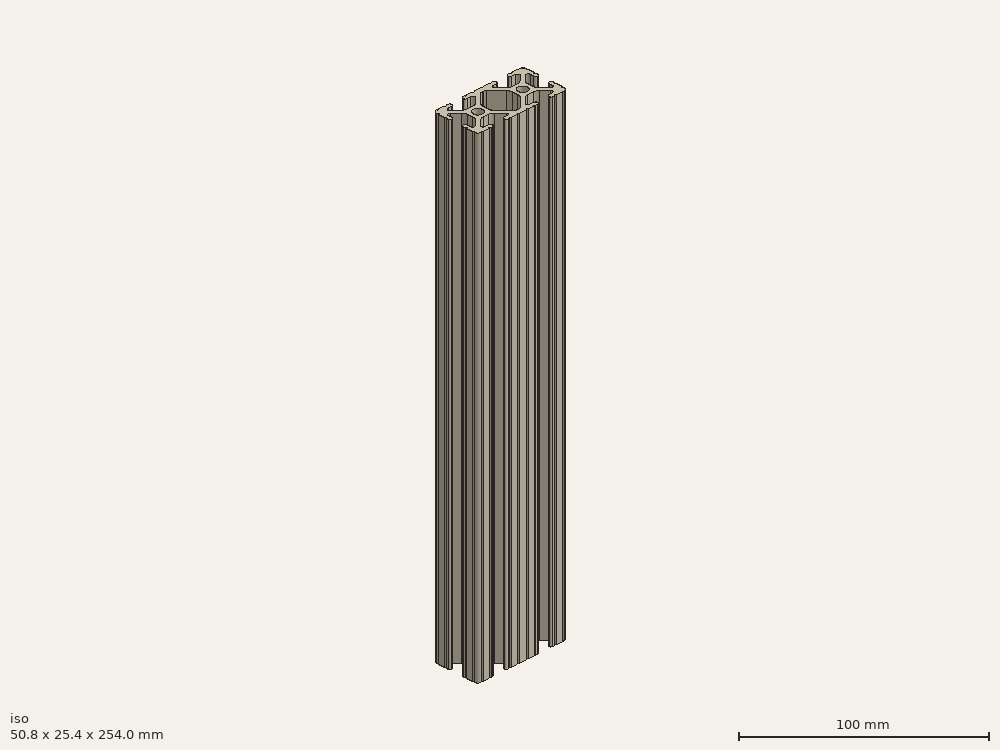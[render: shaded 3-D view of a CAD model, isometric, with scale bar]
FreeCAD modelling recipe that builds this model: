
FCSTD DOCUMENT  (FreeCAD 0.19R23756 (Git))
Label: 1020-10
License: All rights reserved
LicenseURL: http://en.wikipedia.org/wiki/All_rights_reserved
objects: Sketcher::SketchObject×1, Part::Extrusion×1
note: 2 computed .brp shape members not serialized (recipe doc carries the construction recipe); baked Part::Feature solids carry a one-line shape summary decoded from their .brp

FEATURE [Sketcher::SketchObject] Sketch162
  FullyConstrained = false
  sketch-geometry (162):
    g0: LineSegment StartX=7.25951 StartY=3.86941 StartZ=0 EndX=1.54575 EndY=9.57277 EndZ=0
    g1: LineSegment StartX=8.41248 StartY=-10.4902 StartZ=0 EndX=6.28364 EndY=-10.4902 EndZ=0
    g2: ArcOfCircle CenterX=8.41255 CenterY=-11.651 CenterZ=0 NormalX=0 NormalY=0 NormalZ=1 AngleXU=0 Radius=1.04895 StartAngle=4.71239 EndAngle=6.28319
    g3: LineSegment StartX=5.53258 StartY=-8.66607 StartZ=0 EndX=8.80999 EndY=-5.41626 EndZ=0
    g4: LineSegment StartX=9.4615 StartY=-11.651 StartZ=0 EndX=9.4615 EndY=-11.5392 EndZ=0
    g5: ArcOfCircle CenterX=8.41248 CenterY=-11.5392 CenterZ=0 NormalX=0 NormalY=0 NormalZ=1 AngleXU=0 Radius=1.04902 StartAngle=1.15714e-07 EndAngle=1.5708
    g6: ArcOfCircle CenterX=6.28364 CenterY=-9.42351 CenterZ=0 NormalX=0 NormalY=0 NormalZ=1 AngleXU=0 Radius=1.06669 StartAngle=2.35197 EndAngle=4.71239
    g7: LineSegment StartX=-7.28286 StartY=-3.84586 StartZ=0 EndX=-1.67557 EndY=-9.56109 EndZ=0
    g8: LineSegment StartX=1.50403 StartY=-9.57645 StartZ=0 EndX=7.25205 EndY=-3.87684 EndZ=0
    g9: LineSegment StartX=-0.551457 StartY=-10.033 StartZ=0 EndX=0.3952 EndY=-10.033 EndZ=0
    g10: LineSegment StartX=-1.54575 StartY=9.57277 StartZ=0 EndX=-7.25951 EndY=3.86941 EndZ=0
    g11: ArcOfCircle CenterX=0.3952 CenterY=-8.4582 CenterZ=0 NormalX=0 NormalY=0 NormalZ=1 AngleXU=0 Radius=1.5748 StartAngle=4.71239 EndAngle=5.49356
    g12: ArcOfCircle CenterX=5.0165 CenterY=-1.6223 CenterZ=0 NormalX=0 NormalY=0 NormalZ=1 AngleXU=0 Radius=3.175 StartAngle=5.49356 EndAngle=6.28319
    g13: LineSegment StartX=8.1915 StartY=-1.6223 StartZ=0 EndX=8.1915 EndY=1.6223 EndZ=0
    g14: LineSegment StartX=0.433213 StartY=10.033 StartZ=0 EndX=-0.433213 EndY=10.033 EndZ=0
    g15: ArcOfCircle CenterX=-0.551456 CenterY=-8.4582 CenterZ=0 NormalX=0 NormalY=0 NormalZ=1 AngleXU=0 Radius=1.5748 StartAngle=3.91746 EndAngle=4.71239
    g16: ArcOfCircle CenterX=-5.0165 CenterY=1.6223 CenterZ=0 NormalX=0 NormalY=0 NormalZ=1 AngleXU=0 Radius=3.175 StartAngle=2.35528 EndAngle=3.14159
    g17: ArcOfCircle CenterX=-0.433213 CenterY=8.4582 CenterZ=0 NormalX=0 NormalY=0 NormalZ=1 AngleXU=0 Radius=1.5748 StartAngle=1.5708 EndAngle=2.35528
    g18: ArcOfCircle CenterX=5.0165 CenterY=1.6223 CenterZ=0 NormalX=0 NormalY=0 NormalZ=1 AngleXU=0 Radius=3.175 StartAngle=2.15656e-07 EndAngle=0.78631
    g19: Circle CenterX=12.7 CenterY=-2.5e-15 CenterZ=0 NormalX=0 NormalY=0 NormalZ=-1 AngleXU=0 Radius=2.6035
    g20: Circle CenterX=-12.7 CenterY=2.5e-15 CenterZ=0 NormalX=0 NormalY=0 NormalZ=-1 AngleXU=0 Radius=2.6035
    g21: LineSegment StartX=-8.1915 StartY=1.6223 StartZ=0 EndX=-8.1915 EndY=-1.6223 EndZ=0
    g22: LineSegment StartX=-2.13358 StartY=-12.7 StartZ=0 EndX=2.13358 EndY=-12.7 EndZ=0
    g23: ArcOfCircle CenterX=-5.0165 CenterY=-1.6223 CenterZ=0 NormalX=0 NormalY=0 NormalZ=1 AngleXU=0 Radius=3.175 StartAngle=3.14159 EndAngle=3.91746
    g24: LineSegment StartX=3.14958 StartY=-12.7 StartZ=0 EndX=6.3669 EndY=-12.7 EndZ=0
    g25: ArcOfCircle CenterX=6.8749 CenterY=-12.7 CenterZ=0 NormalX=0 NormalY=0 NormalZ=1 AngleXU=0 Radius=0.508 StartAngle=0 EndAngle=3.14159
    g26: LineSegment StartX=-6.28939 StartY=-10.4902 StartZ=0 EndX=-8.41248 EndY=-10.4902 EndZ=0
    g27: LineSegment StartX=-8.41255 StartY=-12.7 StartZ=0 EndX=-7.38288 EndY=-12.7 EndZ=0
    g28: ArcOfCircle CenterX=0.433213 CenterY=8.4582 CenterZ=0 NormalX=0 NormalY=0 NormalZ=1 AngleXU=0 Radius=1.5748 StartAngle=0.78631 EndAngle=1.5708
    g29: ArcOfCircle CenterX=2.64158 CenterY=-12.7 CenterZ=0 NormalX=0 NormalY=0 NormalZ=1 AngleXU=0 Radius=0.508 StartAngle=0 EndAngle=3.14159
    g30: ArcOfCircle CenterX=-16.9875 CenterY=-11.5392 CenterZ=0 NormalX=0 NormalY=0 NormalZ=1 AngleXU=0 Radius=1.04902 StartAngle=1.16223e-07 EndAngle=1.5708
    g31: LineSegment StartX=-8.81696 StartY=-5.44724 StartZ=0 EndX=-5.56415 EndY=-8.76265 EndZ=0
    g32: LineSegment StartX=-16.9875 StartY=-10.4902 StartZ=0 EndX=-19.1164 EndY=-10.4902 EndZ=0
    g33: ArcOfCircle CenterX=-11.0833 CenterY=-7.6708 CenterZ=0 NormalX=0 NormalY=0 NormalZ=1 AngleXU=0 Radius=3.175 StartAngle=0.775866 EndAngle=1.5708
    g34: ArcOfCircle CenterX=-14.3449 CenterY=-7.6708 CenterZ=0 NormalX=0 NormalY=0 NormalZ=1 AngleXU=0 Radius=3.175 StartAngle=1.5708 EndAngle=2.3692
    g35: ArcOfCircle CenterX=-19.1164 CenterY=-9.4742 CenterZ=0 NormalX=0 NormalY=0 NormalZ=1 AngleXU=0 Radius=1.016 StartAngle=2.3692 EndAngle=4.71239
    g36: ArcOfCircle CenterX=-8.41248 CenterY=-11.5392 CenterZ=0 NormalX=0 NormalY=0 NormalZ=1 AngleXU=0 Radius=1.04902 StartAngle=1.5708 EndAngle=3.14159
    g37: LineSegment StartX=7.3829 StartY=-12.7 StartZ=0 EndX=8.41255 EndY=-12.7 EndZ=0
    g38: ArcOfCircle CenterX=-8.41255 CenterY=-11.651 CenterZ=0 NormalX=0 NormalY=0 NormalZ=1 AngleXU=0 Radius=1.04895 StartAngle=3.14159 EndAngle=4.71239
    g39: ArcOfCircle CenterX=14.3545 CenterY=-7.6708 CenterZ=0 NormalX=0 NormalY=0 NormalZ=1 AngleXU=0 Radius=3.175 StartAngle=0.789627 EndAngle=1.5708
    g40: ArcOfCircle CenterX=20.3835 CenterY=-1.55362 CenterZ=0 NormalX=0 NormalY=0 NormalZ=1 AngleXU=0 Radius=3.175 StartAngle=3.14159 EndAngle=3.93122
    g41: LineSegment StartX=23.1902 StartY=6.498 StartZ=0 EndX=23.1902 EndY=4.28752 EndZ=0
    g42: LineSegment StartX=-14.3449 StartY=-4.4958 StartZ=0 EndX=-11.0833 EndY=-4.4958 EndZ=0
    g43: LineSegment StartX=-19.8441 StartY=-8.76517 StartZ=0 EndX=-16.619 EndY=-5.45511 EndZ=0
    g44: LineSegment StartX=-6.36688 StartY=-12.7 StartZ=0 EndX=-3.14958 EndY=-12.7 EndZ=0
    g45: ArcOfCircle CenterX=-6.28939 CenterY=-9.4742 CenterZ=0 NormalX=0 NormalY=0 NormalZ=1 AngleXU=0 Radius=1.016 StartAngle=4.71239 EndAngle=7.05905
    g46: LineSegment StartX=-9.4615 StartY=-11.5392 StartZ=0 EndX=-9.4615 EndY=-11.6511 EndZ=0
    g47: ArcOfCircle CenterX=-6.87488 CenterY=-12.7 CenterZ=0 NormalX=0 NormalY=0 NormalZ=1 AngleXU=0 Radius=0.508 StartAngle=0 EndAngle=3.14159
    g48: LineSegment StartX=-15.9385 StartY=-11.651 StartZ=0 EndX=-15.9385 EndY=-11.5392 EndZ=0
    g49: ArcOfCircle CenterX=-2.64158 CenterY=-12.7 CenterZ=0 NormalX=0 NormalY=0 NormalZ=1 AngleXU=0 Radius=0.508 StartAngle=0 EndAngle=3.14159
    g50: ArcOfCircle CenterX=22.1596 CenterY=-6.33474 CenterZ=0 NormalX=0 NormalY=0 NormalZ=1 AngleXU=0 Radius=1.03057 StartAngle=3.93122 EndAngle=6.28319
    g51: ArcOfCircle CenterX=25.4 CenterY=5.82513 CenterZ=0 NormalX=0 NormalY=0 NormalZ=1 AngleXU=0 Radius=0.508 StartAngle=1.5708 EndAngle=4.71239
    g52: LineSegment StartX=25.4 StartY=6.33313 StartZ=0 EndX=25.4 EndY=9.5504 EndZ=0
    g53: LineSegment StartX=19.0331 StartY=-12.7 StartZ=0 EndX=22.2504 EndY=-12.7 EndZ=0
    g54: ArcOfCircle CenterX=20.3835 CenterY=1.69518 CenterZ=0 NormalX=0 NormalY=0 NormalZ=1 AngleXU=0 Radius=3.175 StartAngle=2.35528 EndAngle=3.14159
    g55: LineSegment StartX=16.9875 StartY=-12.7 StartZ=0 EndX=18.0171 EndY=-12.7 EndZ=0
    g56: ArcOfCircle CenterX=23.2918 CenterY=10.5918 CenterZ=0 NormalX=0 NormalY=0 NormalZ=1 AngleXU=0 Radius=2.1082 StartAngle=6.27114 EndAngle=7.86603
    g57: ArcOfCircle CenterX=24.2392 CenterY=-4.28752 CenterZ=0 NormalX=0 NormalY=0 NormalZ=1 AngleXU=0 Radius=1.04902 StartAngle=1.5708 EndAngle=3.14159
    g58: ArcOfCircle CenterX=24.401 CenterY=-4.23752 CenterZ=0 NormalX=0 NormalY=0 NormalZ=1 AngleXU=0 Radius=0.99902 StartAngle=1.41033e-07 EndAngle=1.5708
    g59: LineSegment StartX=16.59 StartY=-5.41626 StartZ=0 EndX=19.8674 EndY=-8.66607 EndZ=0
    g60: ArcOfCircle CenterX=16.9875 CenterY=-11.5392 CenterZ=0 NormalX=0 NormalY=0 NormalZ=1 AngleXU=0 Radius=1.04902 StartAngle=1.5708 EndAngle=3.14159
    g61: LineSegment StartX=22.2504 StartY=12.7 StartZ=0 EndX=19.0331 EndY=12.7 EndZ=0
    g62: ArcOfCircle CenterX=23.2918 CenterY=-10.5918 CenterZ=0 NormalX=0 NormalY=0 NormalZ=1 AngleXU=0 Radius=2.1082 StartAngle=4.70034 EndAngle=6.29523
    g63: ArcOfCircle CenterX=11.0455 CenterY=-7.6708 CenterZ=0 NormalX=0 NormalY=0 NormalZ=1 AngleXU=0 Radius=3.175 StartAngle=1.5708 EndAngle=2.35197
    g64: ArcOfCircle CenterX=22.7584 CenterY=12.7 CenterZ=0 NormalX=0 NormalY=0 NormalZ=1 AngleXU=0 Radius=0.508 StartAngle=3.14159 EndAngle=6.28288
    g65: LineSegment StartX=19.1164 StartY=-10.4902 StartZ=0 EndX=16.9875 EndY=-10.4902 EndZ=0
    g66: ArcOfCircle CenterX=22.7584 CenterY=-12.7 CenterZ=0 NormalX=0 NormalY=0 NormalZ=1 AngleXU=0 Radius=0.508 StartAngle=0.000301216 EndAngle=3.14159
    g67: ArcOfCircle CenterX=16.9875 CenterY=11.651 CenterZ=0 NormalX=0 NormalY=0 NormalZ=1 AngleXU=0 Radius=1.04902 StartAngle=1.5708 EndAngle=3.14159
    g68: ArcOfCircle CenterX=24.351 CenterY=4.28752 CenterZ=0 NormalX=0 NormalY=0 NormalZ=1 AngleXU=0 Radius=1.04902 StartAngle=4.71239 EndAngle=6.28319
    g69: ArcOfCircle CenterX=19.1164 CenterY=9.4742 CenterZ=0 NormalX=0 NormalY=0 NormalZ=1 AngleXU=0 Radius=1.016 StartAngle=5.49688 EndAngle=7.85398
    g70: LineSegment StartX=19.8341 StartY=8.75512 StartZ=0 EndX=16.4966 EndY=5.42369 EndZ=0
    g71: LineSegment StartX=18.0171 StartY=12.7 StartZ=0 EndX=16.9875 EndY=12.7 EndZ=0
    g72: ArcOfCircle CenterX=18.5251 CenterY=-12.7 CenterZ=0 NormalX=0 NormalY=0 NormalZ=1 AngleXU=0 Radius=0.508 StartAngle=0 EndAngle=3.14159
    g73: LineSegment StartX=15.9384 StartY=11.651 StartZ=0 EndX=15.9384 EndY=11.5392 EndZ=0
    g74: LineSegment StartX=16.9875 StartY=10.4902 StartZ=0 EndX=19.1164 EndY=10.4902 EndZ=0
    g75: LineSegment StartX=11.0455 StartY=-4.4958 StartZ=0 EndX=14.3545 EndY=-4.4958 EndZ=0
    g76: ArcOfCircle CenterX=14.2536 CenterY=7.6708 CenterZ=0 NormalX=0 NormalY=0 NormalZ=1 AngleXU=0 Radius=3.175 StartAngle=4.71239 EndAngle=5.49688
    g77: ArcOfCircle CenterX=25.4 CenterY=-5.82508 CenterZ=0 NormalX=0 NormalY=0 NormalZ=1 AngleXU=0 Radius=0.508 StartAngle=1.5708 EndAngle=4.71239
    g78: LineSegment StartX=18.1405 StartY=3.94229 StartZ=0 EndX=21.4316 EndY=7.22739 EndZ=0
    g79: LineSegment StartX=25.4 StartY=-5.31708 StartZ=0 EndX=25.4 EndY=-4.23752 EndZ=0
    g80: LineSegment StartX=14.2536 StartY=4.4958 StartZ=0 EndX=11.1464 EndY=4.4958 EndZ=0
    g81: ArcOfCircle CenterX=18.5251 CenterY=12.7 CenterZ=0 NormalX=0 NormalY=0 NormalZ=1 AngleXU=0 Radius=0.508 StartAngle=3.14159 EndAngle=6.28319
    g82: LineSegment StartX=23.1902 StartY=-4.28752 StartZ=0 EndX=23.1902 EndY=-6.33474 EndZ=0
    g83: LineSegment StartX=24.401 StartY=-3.2385 StartZ=0 EndX=24.2392 EndY=-3.2385 EndZ=0
    g84: ArcOfCircle CenterX=22.1596 CenterY=6.498 CenterZ=0 NormalX=0 NormalY=0 NormalZ=1 AngleXU=0 Radius=1.03057 StartAngle=0 EndAngle=2.35528
    g85: LineSegment StartX=15.9385 StartY=-11.5392 StartZ=0 EndX=15.9385 EndY=-11.6511 EndZ=0
    g86: LineSegment StartX=25.4 StartY=4.28752 StartZ=0 EndX=25.4 EndY=5.31713 EndZ=0
    g87: ArcOfCircle CenterX=11.1464 CenterY=7.6708 CenterZ=0 NormalX=0 NormalY=0 NormalZ=1 AngleXU=0 Radius=3.175 StartAngle=3.9279 EndAngle=4.71239
    g88: LineSegment StartX=8.90339 StartY=5.42369 StartZ=0 EndX=5.56588 EndY=8.75512 EndZ=0
    g89: LineSegment StartX=21.434 StartY=-7.06654 StartZ=0 EndX=18.148 EndY=-3.80816 EndZ=0
    g90: ArcOfCircle CenterX=25.4 CenterY=10.0584 CenterZ=0 NormalX=0 NormalY=0 NormalZ=1 AngleXU=0 Radius=0.508 StartAngle=1.5711 EndAngle=4.71239
    g91: ArcOfCircle CenterX=16.9875 CenterY=-11.651 CenterZ=0 NormalX=0 NormalY=0 NormalZ=1 AngleXU=0 Radius=1.04895 StartAngle=3.14159 EndAngle=4.71239
    g92: ArcOfCircle CenterX=19.1164 CenterY=-9.42352 CenterZ=0 NormalX=0 NormalY=0 NormalZ=1 AngleXU=0 Radius=1.06668 StartAngle=4.71239 EndAngle=7.07281
    g93: ArcOfCircle CenterX=24.2392 CenterY=4.28752 CenterZ=0 NormalX=0 NormalY=0 NormalZ=1 AngleXU=0 Radius=1.04902 StartAngle=3.14159 EndAngle=4.71239
    g94: ArcOfCircle CenterX=16.9875 CenterY=11.5392 CenterZ=0 NormalX=0 NormalY=0 NormalZ=1 AngleXU=0 Radius=1.04902 StartAngle=3.14159 EndAngle=4.71239
    g95: ArcOfCircle CenterX=25.4 CenterY=-10.0584 CenterZ=0 NormalX=0 NormalY=0 NormalZ=1 AngleXU=0 Radius=0.508 StartAngle=1.5708 EndAngle=4.71209
    g96: ArcOfCircle CenterX=6.87487 CenterY=12.7 CenterZ=0 NormalX=0 NormalY=0 NormalZ=1 AngleXU=0 Radius=0.508 StartAngle=3.14159 EndAngle=6.28319
    g97: LineSegment StartX=25.4 StartY=-9.5504 StartZ=0 EndX=25.4 EndY=-6.33308 EndZ=0
    g98: LineSegment StartX=17.2085 StartY=-1.55362 StartZ=0 EndX=17.2085 EndY=1.69518 EndZ=0
    g99: LineSegment StartX=-9.46155 StartY=11.651 StartZ=0 EndX=-9.46155 EndY=11.5392 EndZ=0
    g100: LineSegment StartX=24.2392 StartY=3.2385 StartZ=0 EndX=24.351 EndY=3.2385 EndZ=0
    g101: LineSegment StartX=-8.41253 StartY=10.4902 StartZ=0 EndX=-6.28939 EndY=10.4902 EndZ=0
    g102: ArcOfCircle CenterX=-10.8409 CenterY=7.6708 CenterZ=0 NormalX=0 NormalY=0 NormalZ=1 AngleXU=0 Radius=3.175 StartAngle=4.71239 EndAngle=5.49688
    g103: LineSegment StartX=-19.1164 StartY=10.4902 StartZ=0 EndX=-16.9875 EndY=10.4902 EndZ=0
    g104: LineSegment StartX=-10.8409 StartY=4.4958 StartZ=0 EndX=-14.1026 EndY=4.4958 EndZ=0
    g105: LineSegment StartX=-16.1879 StartY=5.27664 StartZ=0 EndX=-19.8682 EndY=8.48225 EndZ=0
    g106: LineSegment StartX=-7.38291 StartY=12.7 StartZ=0 EndX=-8.41253 EndY=12.7 EndZ=0
    g107: ArcOfCircle CenterX=-6.28939 CenterY=9.34546 CenterZ=0 NormalX=0 NormalY=0 NormalZ=1 AngleXU=0 Radius=1.14474 StartAngle=5.49688 EndAngle=7.85398
    g108: LineSegment StartX=6.28364 StartY=10.4902 StartZ=0 EndX=8.41253 EndY=10.4902 EndZ=0
    g109: ArcOfCircle CenterX=8.41253 CenterY=11.651 CenterZ=0 NormalX=0 NormalY=0 NormalZ=1 AngleXU=0 Radius=1.04902 StartAngle=4.29175e-07 EndAngle=1.5708
    g110: LineSegment StartX=9.46155 StartY=11.5392 StartZ=0 EndX=9.46155 EndY=11.651 EndZ=0
    g111: ArcOfCircle CenterX=-14.1026 CenterY=7.6708 CenterZ=0 NormalX=0 NormalY=0 NormalZ=1 AngleXU=0 Radius=3.175 StartAngle=3.99583 EndAngle=4.71239
    g112: LineSegment StartX=-5.48068 StartY=8.53527 StartZ=0 EndX=-8.59793 EndY=5.42369 EndZ=0
    g113: ArcOfCircle CenterX=-19.1164 CenterY=9.34546 CenterZ=0 NormalX=0 NormalY=0 NormalZ=1 AngleXU=0 Radius=1.14474 StartAngle=1.5708 EndAngle=3.99583
    g114: LineSegment StartX=8.41253 StartY=12.7 StartZ=0 EndX=7.38287 EndY=12.7 EndZ=0
    g115: LineSegment StartX=-3.14958 StartY=12.7 StartZ=0 EndX=-6.36691 EndY=12.7 EndZ=0
    g116: ArcOfCircle CenterX=-8.41253 CenterY=11.5392 CenterZ=0 NormalX=0 NormalY=0 NormalZ=1 AngleXU=0 Radius=1.04902 StartAngle=3.14159 EndAngle=4.71239
    g117: ArcOfCircle CenterX=8.41253 CenterY=11.5392 CenterZ=0 NormalX=0 NormalY=0 NormalZ=1 AngleXU=0 Radius=1.04902 StartAngle=4.71239 EndAngle=6.28319
    g118: ArcOfCircle CenterX=-6.87491 CenterY=12.7 CenterZ=0 NormalX=0 NormalY=0 NormalZ=1 AngleXU=0 Radius=0.508 StartAngle=3.14159 EndAngle=6.28319
    g119: ArcOfCircle CenterX=-8.41253 CenterY=11.651 CenterZ=0 NormalX=0 NormalY=0 NormalZ=1 AngleXU=0 Radius=1.04902 StartAngle=1.5708 EndAngle=3.14159
    g120: ArcOfCircle CenterX=-2.64159 CenterY=12.7 CenterZ=0 NormalX=0 NormalY=0 NormalZ=1 AngleXU=0 Radius=0.507987 StartAngle=3.14159 EndAngle=6.28319
    g121: ArcOfCircle CenterX=6.28364 CenterY=9.4742 CenterZ=0 NormalX=0 NormalY=0 NormalZ=1 AngleXU=0 Radius=1.016 StartAngle=1.5708 EndAngle=3.9279
    g122: LineSegment StartX=2.13361 StartY=12.7 StartZ=0 EndX=-2.13361 EndY=12.7 EndZ=0
    g123: LineSegment StartX=6.36687 StartY=12.7 StartZ=0 EndX=3.14961 EndY=12.7 EndZ=0
    g124: ArcOfCircle CenterX=-24.401 CenterY=4.23752 CenterZ=0 NormalX=0 NormalY=0 NormalZ=1 AngleXU=0 Radius=0.99902 StartAngle=3.14159 EndAngle=4.71239
    g125: LineSegment StartX=-16.9875 StartY=12.7 StartZ=0 EndX=-18.0171 EndY=12.7 EndZ=0
    g126: LineSegment StartX=-24.401 StartY=3.2385 StartZ=0 EndX=-24.1892 EndY=3.2385 EndZ=0
    g127: ArcOfCircle CenterX=2.64161 CenterY=12.7 CenterZ=0 NormalX=0 NormalY=0 NormalZ=1 AngleXU=0 Radius=0.508 StartAngle=3.14159 EndAngle=6.28319
    g128: ArcOfCircle CenterX=-22.2207 CenterY=-6.67687 CenterZ=0 NormalX=0 NormalY=0 NormalZ=1 AngleXU=0 Radius=0.969476 StartAngle=3.14159 EndAngle=5.51079
    g129: LineSegment StartX=-18.1094 StartY=-3.8465 StartZ=0 EndX=-21.5263 EndY=-7.35342 EndZ=0
    g130: LineSegment StartX=-17.2085 StartY=1.63081 StartZ=0 EndX=-17.2085 EndY=-1.63081 EndZ=0
    g131: ArcOfCircle CenterX=-22.2207 CenterY=6.15588 CenterZ=0 NormalX=0 NormalY=0 NormalZ=1 AngleXU=0 Radius=0.969476 StartAngle=0.854233 EndAngle=3.14159
    g132: LineSegment StartX=-24.1892 StartY=-3.2385 StartZ=0 EndX=-24.401 EndY=-3.2385 EndZ=0
    g133: ArcOfCircle CenterX=-25.4 CenterY=10.0584 CenterZ=0 NormalX=0 NormalY=0 NormalZ=1 AngleXU=0 Radius=0.508 StartAngle=4.71239 EndAngle=7.85368
    g134: LineSegment StartX=-23.1902 StartY=-6.67687 StartZ=0 EndX=-23.1902 EndY=-4.23752 EndZ=0
    g135: ArcOfCircle CenterX=-20.3835 CenterY=-1.63081 CenterZ=0 NormalX=0 NormalY=0 NormalZ=1 AngleXU=0 Radius=3.175 StartAngle=5.51079 EndAngle=6.28319
    g136: ArcOfCircle CenterX=-24.1892 CenterY=-4.23752 CenterZ=0 NormalX=0 NormalY=0 NormalZ=1 AngleXU=0 Radius=0.99902 StartAngle=1.41033e-07 EndAngle=1.5708
    g137: ArcOfCircle CenterX=-25.4 CenterY=5.82508 CenterZ=0 NormalX=0 NormalY=0 NormalZ=1 AngleXU=0 Radius=0.508 StartAngle=4.71239 EndAngle=7.85398
    g138: LineSegment StartX=-23.1902 StartY=4.23752 StartZ=0 EndX=-23.1902 EndY=6.15588 EndZ=0
    g139: LineSegment StartX=-15.9384 StartY=11.5392 StartZ=0 EndX=-15.9384 EndY=11.651 EndZ=0
    g140: ArcOfCircle CenterX=-22.7584 CenterY=12.7 CenterZ=0 NormalX=0 NormalY=0 NormalZ=1 AngleXU=0 Radius=0.508 StartAngle=3.14189 EndAngle=6.28319
    g141: LineSegment StartX=-19.0331 StartY=12.7 StartZ=0 EndX=-22.2504 EndY=12.7 EndZ=0
    g142: ArcOfCircle CenterX=-16.9875 CenterY=11.651 CenterZ=0 NormalX=0 NormalY=0 NormalZ=1 AngleXU=0 Radius=1.04902 StartAngle=4.28571e-07 EndAngle=1.5708
    g143: ArcOfCircle CenterX=-18.5251 CenterY=12.7 CenterZ=0 NormalX=0 NormalY=0 NormalZ=1 AngleXU=0 Radius=0.508 StartAngle=3.14159 EndAngle=6.28319
    g144: ArcOfCircle CenterX=-24.1892 CenterY=4.23752 CenterZ=0 NormalX=0 NormalY=0 NormalZ=1 AngleXU=0 Radius=0.99902 StartAngle=4.71239 EndAngle=6.28319
    g145: LineSegment StartX=-25.4 StartY=5.31708 StartZ=0 EndX=-25.4 EndY=4.23752 EndZ=0
    g146: ArcOfCircle CenterX=-16.9875 CenterY=11.5392 CenterZ=0 NormalX=0 NormalY=0 NormalZ=1 AngleXU=0 Radius=1.04902 StartAngle=4.71239 EndAngle=6.28319
    g147: LineSegment StartX=-21.584 StartY=6.88693 StartZ=0 EndX=-18.2982 EndY=4.02497 EndZ=0
    g148: ArcOfCircle CenterX=-20.3835 CenterY=1.63081 CenterZ=0 NormalX=0 NormalY=0 NormalZ=1 AngleXU=0 Radius=3.175 StartAngle=0 EndAngle=0.854233
    g149: ArcOfCircle CenterX=-23.2918 CenterY=10.5918 CenterZ=0 NormalX=0 NormalY=0 NormalZ=1 AngleXU=0 Radius=2.1082 StartAngle=1.55875 EndAngle=3.15364
    g150: LineSegment StartX=-25.4 StartY=9.5504 StartZ=0 EndX=-25.4 EndY=6.33308 EndZ=0
    g151: LineSegment StartX=-25.4 StartY=-4.23752 StartZ=0 EndX=-25.4 EndY=-5.31708 EndZ=0
    g152: ArcOfCircle CenterX=-23.2918 CenterY=-10.5918 CenterZ=0 NormalX=0 NormalY=0 NormalZ=1 AngleXU=0 Radius=2.1082 StartAngle=3.12954 EndAngle=4.72444
    g153: ArcOfCircle CenterX=-22.7584 CenterY=-12.7 CenterZ=0 NormalX=0 NormalY=0 NormalZ=1 AngleXU=0 Radius=0.508 StartAngle=0 EndAngle=3.14129
    g154: LineSegment StartX=-18.0171 StartY=-12.7 StartZ=0 EndX=-16.9875 EndY=-12.7 EndZ=0
    g155: ArcOfCircle CenterX=-25.4 CenterY=-10.0584 CenterZ=0 NormalX=0 NormalY=0 NormalZ=1 AngleXU=0 Radius=0.508 StartAngle=4.71269 EndAngle=7.85398
    g156: LineSegment StartX=-22.2504 StartY=-12.7 StartZ=0 EndX=-19.0331 EndY=-12.7 EndZ=0
    g157: ArcOfCircle CenterX=-16.9875 CenterY=-11.651 CenterZ=0 NormalX=0 NormalY=0 NormalZ=1 AngleXU=0 Radius=1.04895 StartAngle=4.71239 EndAngle=6.28319
    g158: ArcOfCircle CenterX=-24.401 CenterY=-4.23752 CenterZ=0 NormalX=0 NormalY=0 NormalZ=1 AngleXU=0 Radius=0.99902 StartAngle=1.5708 EndAngle=3.14159
    g159: ArcOfCircle CenterX=-25.4 CenterY=-5.82513 CenterZ=0 NormalX=0 NormalY=0 NormalZ=1 AngleXU=0 Radius=0.508051 StartAngle=4.71239 EndAngle=7.85398
    g160: ArcOfCircle CenterX=-18.5251 CenterY=-12.7 CenterZ=0 NormalX=0 NormalY=0 NormalZ=1 AngleXU=0 Radius=0.508 StartAngle=0 EndAngle=3.14159
    g161: LineSegment StartX=-25.4 StartY=-6.33319 StartZ=0 EndX=-25.4 EndY=-9.5504 EndZ=0
  constraints (160):
    c: Coincident(g161,g155)
    c: Coincident(g159,g161)
    c: Coincident(g151,g159)
    c: Coincident(g158,g151)
    c: Coincident(g124,g145)
    c: Coincident(g137,g145)
    c: Coincident(g137,g150)
    c: Coincident(g133,g150)
    c: Coincident(g152,g155)
    c: Coincident(g149,g133)
    c: Coincident(g158,g132)
    c: Coincident(g124,g126)
    c: Coincident(g136,g132)
    c: Coincident(g144,g126)
    c: Coincident(g153,g152)
    c: Coincident(g140,g149)
    c: Coincident(g134,g128)
    c: Coincident(g134,g136)
    c: Coincident(g138,g144)
    c: Coincident(g131,g138)
    c: Coincident(g153,g156)
    c: Coincident(g141,g140)
    c: Coincident(g131,g147)
    c: Coincident(g129,g128)
    c: Coincident(g105,g113)
    c: Coincident(g35,g43)
    c: Coincident(g35,g32)
    c: Coincident(g113,g103)
    c: Coincident(g156,g160)
    c: Coincident(g143,g141)
    c: Coincident(g147,g148)
    c: Coincident(g135,g129)
    c: Coincident(g154,g160)
    c: Coincident(g143,g125)
    c: Coincident(g130,g135)
    c: Coincident(g130,g148)
    c: Coincident(g154,g157)
    c: Coincident(g32,g30)
    c: Coincident(g103,g146)
    c: Coincident(g142,g125)
    c: Coincident(g43,g34)
    c: Coincident(g111,g105)
    c: Coincident(g157,g48)
    c: Coincident(g48,g30)
    c: Coincident(g139,g146)
    c: Coincident(g139,g142)
    c: Coincident(g42,g34)
    c: Coincident(g104,g111)
    c: Coincident(g33,g42)
    c: Coincident(g102,g104)
    c: Coincident(g38,g46)
    c: Coincident(g46,g36)
    c: Coincident(g99,g116)
    c: Coincident(g119,g99)
    c: Coincident(g33,g31)
    c: Coincident(g102,g112)
    c: Coincident(g27,g38)
    c: Coincident(g36,g26)
    c: Coincident(g116,g101)
    c: Coincident(g106,g119)
    c: Coincident(g21,g23)
    c: Coincident(g21,g16)
    c: Coincident(g27,g47)
    c: Coincident(g106,g118)
    c: Coincident(g23,g7)
    c: Coincident(g10,g16)
    c: Coincident(g44,g47)
    c: Coincident(g118,g115)
    c: Coincident(g45,g26)
    c: Coincident(g107,g101)
    c: Coincident(g45,g31)
    c: Coincident(g112,g107)
    c: Coincident(g44,g49)
    c: Coincident(g120,g115)
    c: Coincident(g22,g49)
    c: Coincident(g122,g120)
    c: Coincident(g15,g7)
    c: Coincident(g10,g17)
    c: Coincident(g9,g15)
    c: Coincident(g17,g14)
    c: Coincident(g9,g11)
    c: Coincident(g14,g28)
    c: Coincident(g8,g11)
    c: Coincident(g0,g28)
    c: Coincident(g29,g22)
    c: Coincident(g122,g127)
    c: Coincident(g24,g29)
    c: Coincident(g123,g127)
    c: Coincident(g3,g6)
    c: Coincident(g88,g121)
    c: Coincident(g1,g6)
    c: Coincident(g108,g121)
    c: Coincident(g25,g24)
    c: Coincident(g96,g123)
    c: Coincident(g8,g12)
    c: Coincident(g18,g0)
    c: Coincident(g25,g37)
    c: Coincident(g96,g114)
    c: Coincident(g12,g13)
    c: Coincident(g18,g13)
    c: Coincident(g2,g37)
    c: Coincident(g5,g1)
    c: Coincident(g117,g108)
    c: Coincident(g109,g114)
    c: Coincident(g3,g63)
    c: Coincident(g87,g88)
    c: Coincident(g2,g4)
    c: Coincident(g5,g4)
    c: Coincident(g117,g110)
    c: Coincident(g109,g110)
    c: Coincident(g75,g63)
    c: Coincident(g80,g87)
    c: Coincident(g80,g76)
    c: Coincident(g39,g75)
    c: Coincident(g85,g91)
    c: Coincident(g85,g60)
    c: Coincident(g73,g94)
    c: Coincident(g73,g67)
    c: Coincident(g70,g76)
    c: Coincident(g59,g39)
    c: Coincident(g55,g91)
    c: Coincident(g60,g65)
    c: Coincident(g94,g74)
    c: Coincident(g67,g71)
    c: Coincident(g40,g98)
    c: Coincident(g54,g98)
    c: Coincident(g55,g72)
    c: Coincident(g71,g81)
    c: Coincident(g78,g54)
    c: Coincident(g40,g89)
    c: Coincident(g53,g72)
    c: Coincident(g61,g81)
    c: Coincident(g65,g92)
    c: Coincident(g74,g69)
    c: Coincident(g70,g69)
    c: Coincident(g59,g92)
    c: Coincident(g84,g78)
    c: Coincident(g50,g89)
    c: Coincident(g53,g66)
    c: Coincident(g64,g61)
    c: Coincident(g82,g50)
    c: Coincident(g57,g82)
    c: Coincident(g41,g93)
    c: Coincident(g41,g84)
    c: Coincident(g62,g66)
    c: Coincident(g64,g56)
    c: Coincident(g57,g83)
    c: Coincident(g100,g93)
    c: Coincident(g100,g68)
    c: Coincident(g58,g83)
    c: Coincident(g62,g95)
    c: Coincident(g56,g90)
    c: Coincident(g97,g95)
    c: Coincident(g97,g77)
    c: Coincident(g77,g79)
    c: Coincident(g58,g79)
    c: Coincident(g68,g86)
    c: Coincident(g86,g51)
    c: Coincident(g51,g52)
    c: Coincident(g52,g90)
FEATURE [Part::Extrusion] Extrude
  Base = -> Sketch162
  Dir = (0,0,1)
  DirMode = 2
  FaceMakerClass = Part::FaceMakerBullseye
  LengthFwd = 254
  LengthRev = 0
  Solid = true
  Symmetric = false
